# Revit family: Universal Column
name_source: partatom
category: Structural Columns
revit_build: Autodesk Revit 2014 (Build: 20131024_2115(x64)
units: mm (PartAtom-declared; Revit-internal decimal feet)

## types (13) — shared parameters

## per-type parameters (varying)
| type | A | Type Comments | W | bf | d | k | kr | tf | tw |
| 250UC72.9 | 0.01 m² | 250UC73 | 0.714905 | 254 mm | 254 mm | 28 mm | 14 mm  [stored 0.0459318 ft] | 14 mm  [stored 0.0459318 ft] | 9 mm  [stored 0.0295276 ft] |
| 200UC46.2 | 0.01 m² | 200UC46 | 0.453067 | 203 mm  [stored 0.66601 ft] | 203 mm  [stored 0.66601 ft] | 22 mm | 11 mm  [stored 0.0360892 ft] | 11 mm  [stored 0.0360892 ft] | 7 mm  [stored 0.0229659 ft] |
| 150UC23.4 | 0 m² | 150UC23 | 0.229476 | 152 mm  [stored 0.498688 ft] | 152 mm  [stored 0.498688 ft] | 16 mm | 9 mm  [stored 0.0295276 ft] | 7 mm  [stored 0.0229659 ft] | 6 mm  [stored 0.019685 ft] |
| 310UC96.8 | 0.01 m² | 310UC97 | 0.949284 | 305 mm | 308 mm | 32 mm | 17 mm | 15 mm | 10 mm  [stored 0.0328084 ft] |
| 100UC14.8 | 0 m² | 100UC15 | 0.145138 | 99 mm  [stored 0.324803 ft] | 97 mm  [stored 0.318241 ft] | 17 mm | 10 mm  [stored 0.0328084 ft] | 7 mm  [stored 0.0229659 ft] | 5 mm  [stored 0.0164042 ft] |
| 310UC158 | 0.02 m² | 310UC158 | 1.549451 | 311 mm | 327 mm | 42 mm | 17 mm | 25 mm  [stored 0.082021 ft] | 16 mm |
| 310UC137 | 0.02 m² | 310UC137 | 1.343511 | 309 mm | 321 mm | 38 mm | 17 mm | 22 mm | 14 mm  [stored 0.0459318 ft] |
| 310UC118 | 0.02 m² | 310UC118 | 1.157185 | 307 mm | 315 mm | 35 mm | 17 mm | 19 mm | 12 mm |
| 250UC89.5 | 0.01 m² | 250UC89 | 0.877695 | 256 mm  [stored 0.839895 ft] | 260 mm | 31 mm | 14 mm  [stored 0.0459318 ft] | 17 mm | 11 mm  [stored 0.0360892 ft] |
| 200UC59.3 | 0.01 m² | 200UC59 | 0.581534 | 205 mm  [stored 0.672572 ft] | 210 mm  [stored 0.688976 ft] | 26 mm | 11 mm  [stored 0.0360892 ft] | 14 mm  [stored 0.0459318 ft] | 9 mm  [stored 0.0295276 ft] |
| 200UC52.2 | 0.01 m² | 200UC52 | 0.511907 | 204 mm | 206 mm  [stored 0.675853 ft] | 24 mm | 11 mm  [stored 0.0360892 ft] | 13 mm | 8 mm  [stored 0.0262467 ft] |
| 150UC37.2 | 0.01 m² | 150UC37 | 0.364807 | 154 mm  [stored 0.505249 ft] | 162 mm  [stored 0.531496 ft] | 20 mm | 9 mm  [stored 0.0295276 ft] | 12 mm | 8 mm  [stored 0.0262467 ft] |
| 150UC30 | 0 m² | 150UC30 | 0.2942 | 153 mm  [stored 0.501969 ft] | 158 mm | 18 mm | 9 mm  [stored 0.0295276 ft] | 9 mm  [stored 0.0295276 ft] | 7 mm  [stored 0.0229659 ft] |

note: [stored X ft] marks values corroborated as IEEE doubles in the binary element streams (Revit-internal decimal feet)

## geometry (parser evidence)
native form markers: Blend x4
no freeform markers — native parametric forms only
